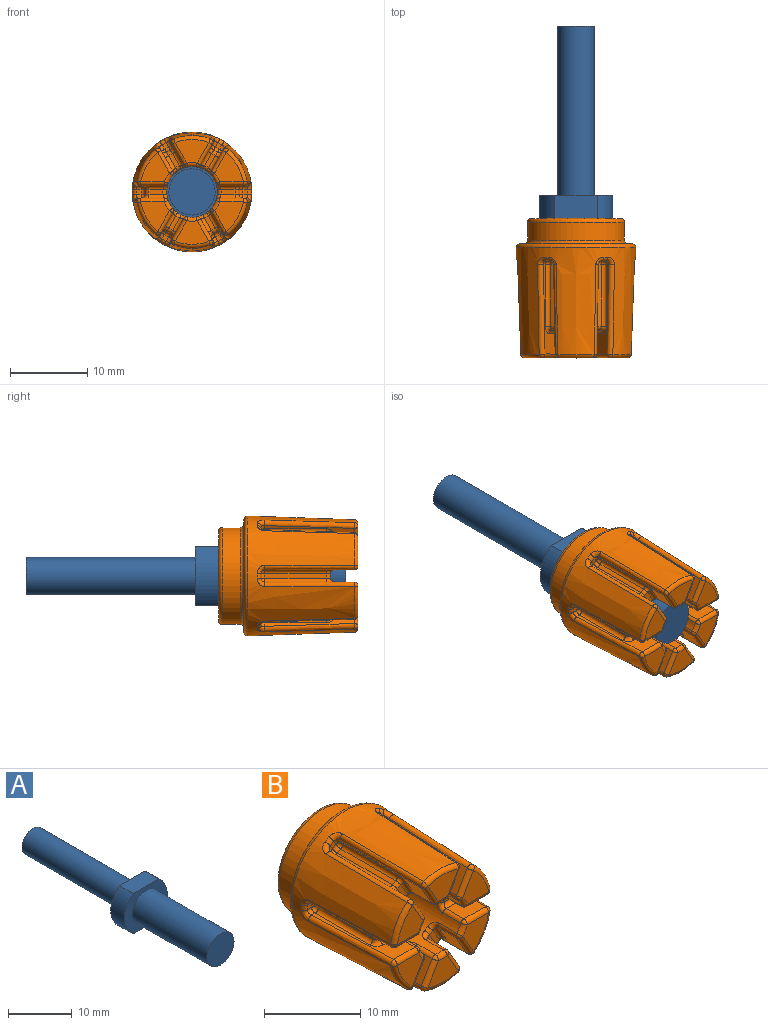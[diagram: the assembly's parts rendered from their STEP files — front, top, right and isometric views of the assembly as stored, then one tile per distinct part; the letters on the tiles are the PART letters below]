
ASSEMBLY  parts=2 mates=1
PART A: 10 faces, bbox 9.5x41.5x7.7 mm
  f0: plane 5.56x3mm, normal (0,0,-1), area 16.7mm2, adj f1,f2,f3,f4
  f1: cylinder r=4.75mm len=7.7mm, axis (0,1,0), area 26.9mm2, adj f0,f3,f4,f5
  f2: cylinder r=4.75mm len=7.7mm, axis (0,1,0), area 26.9mm2, adj f0,f3,f4,f5
  f3: plane 9.5x7.7mm, normal (0,-1,0), area 35.8mm2, adj f0,f1,f2,f5,f8
  f4: plane 9.5x7.7mm, normal (0,1,0), area 46mm2, adj f0,f1,f2,f5,f6
  f5: plane 5.56x3mm, normal (0,0,1), area 16.7mm2, adj f1,f2,f3,f4
  f6: cylinder r=2.4mm len=22mm, axis (0,-1,0), area 331.8mm2, adj f4,f7
  f7: plane 4.8x4.8mm, normal (0,1,0), area 18.1mm2, adj f6
  f8: cylinder r=3mm len=16.5mm, axis (0,1,0), area 311mm2, adj f3,f9
  f9: plane 6x6mm, normal (0,-1,0), area 28.3mm2, adj f8
PART B: 225 faces, bbox 16.8x20.8x16.8 mm
  f0: cone r=7.8mm half-angle=2deg, axis (0,1,0), area 445mm2, adj f49,f50,f53,f54,f58,f63,f69,f75
  f1: plane 11.6x3.05mm, normal (-0.87,0,0.5), area 11.4mm2, adj f194,f195,f207,f208,f213,f216,f217
  f2: plane 11.6x3.05mm, normal (0.87,0,-0.5), area 11.4mm2, adj f186,f187,f203,f204,f210,f214,f215
  f3: plane 1.86x1.42mm, normal (0,-1,0), area 1.1mm2, adj f209,f214,f217,f220
  f4: plane 1.81x0.6mm, normal (0,-1,0), area 1.1mm2, adj f158,f159,f174,f175
  f5: plane 1.86x1.42mm, normal (0,-1,0), area 1.1mm2, adj f98,f99,f114,f115
  f6: plane 1.86x1.42mm, normal (0,-1,0), area 1.1mm2, adj f46,f55,f56,f57
  f7: plane 1.81x0.6mm, normal (0,-1,0), area 1.1mm2, adj f102,f103,f116,f117
  f8: plane 11.6x3.05mm, normal (0.87,0,0.5), area 11.4mm2, adj f164,f165,f171,f177,f178,f191,f192
  f9: plane 11.6x3.05mm, normal (-0.87,0,-0.5), area 11.4mm2, adj f142,f143,f145,f146,f152,f161,f162
  f10: plane 11.6x3.52mm, normal (0,0,-1), area 11.4mm2, adj f82,f83,f85,f86,f92,f101,f102
  f11: plane 11.6x3.05mm, normal (-0.87,0,0.5), area 11.4mm2, adj f47,f48,f52,f57,f58,f66,f67
  f12: plane 11.6x3.05mm, normal (0.87,0,-0.5), area 11.4mm2, adj f44,f45,f51,f54,f55,f64,f65
  f13: plane 11.6x3.05mm, normal (-0.87,0,-0.5), area 11.4mm2, adj f75,f76,f78,f79,f89,f99,f100
  f14: plane 11.6x3.05mm, normal (0.87,0,0.5), area 11.4mm2, adj f96,f97,f108,f113,f114,f124,f125
  f15: plane 4.42x3.06mm, normal (0,-1,0), area 8.8mm2, adj f192,f193,f206,f207
  f16: plane 11.6x3.52mm, normal (0,0,1), area 11.4mm2, adj f104,f105,f111,f117,f118,f126,f127
  f17: plane 3.83x3.76mm, normal (0,-1,0), area 8.8mm2, adj f127,f129,f141,f142
  f18: plane 3.83x3.76mm, normal (0,-1,0), area 8.8mm2, adj f67,f69,f81,f82
  f19: plane 4.42x3.06mm, normal (0,-1,0), area 8.8mm2, adj f63,f64,f79,f80
  f20: plane 11.6x3.52mm, normal (0,0,-1), area 11.4mm2, adj f135,f136,f138,f139,f149,f159,f160
  f21: plane 3.83x3.76mm, normal (0,-1,0), area 8.8mm2, adj f123,f124,f139,f140
  f22: plane 11.6x3.52mm, normal (0,0,1), area 11.4mm2, adj f156,f157,f168,f173,f174,f189,f190
  f23: plane 3.83x3.76mm, normal (0,-1,0), area 8.8mm2, adj f188,f189,f204,f205
  f24: plane 0.86x0.84mm, normal (0,-1,0), area 0.4mm2, adj f179,f186,f195,f196
  f25: plane 1.86x1.42mm, normal (0,-1,0), area 1.1mm2, adj f162,f163,f176,f177
  f26: plane 0.86x0.84mm, normal (0,-1,0), area 0.4mm2, adj f144,f145,f165,f166
  f27: plane 0.65x0.6mm, normal (0,-1,0), area 0.4mm2, adj f84,f85,f105,f106
  f28: plane 0.86x0.84mm, normal (0,-1,0), area 0.4mm2, adj f41,f44,f48,f49
  f29: plane 0.86x0.84mm, normal (0,-1,0), area 0.4mm2, adj f76,f77,f95,f96
  f30: plane 0.65x0.6mm, normal (0,-1,0), area 0.4mm2, adj f136,f137,f155,f156
  f31: cylinder r=6.3mm len=12.6mm, axis (0,1,0), area 91mm2, adj f223,f224
  f32: plane 11.6x11.6mm, normal (0,1,0), area 60.3mm2, adj f221,f223
  f33: plane 14.56x14.56mm, normal (0,1,0), area 21.3mm2, adj f222,f224
  f34: cylinder r=6.1mm len=8mm, axis (0,1,0), area 4.4mm2, adj f137,f138,f157,f158
  f35: cylinder r=6.1mm len=8mm, axis (0,1,0), area 4.4mm2, adj f77,f78,f97,f98
  f36: cylinder r=6.1mm len=8mm, axis (0,1,0), area 4.4mm2, adj f41,f45,f46,f47
  f37: cylinder r=6.1mm len=8mm, axis (0,1,0), area 4.4mm2, adj f83,f84,f103,f104
  f38: cylinder r=6.1mm len=8mm, axis (0,1,0), area 4.4mm2, adj f143,f144,f163,f164
  f39: cylinder r=6.1mm len=8mm, axis (0,1,0), area 4.4mm2, adj f196,f203,f208,f209
  f40: cylinder r=3.3mm len=17.1mm, axis (0,1,0), area 307.1mm2, adj f56,f60,f61,f65,f66,f80,f81,f100
  f41: torus R=6.6mm, axis (0,-1,0), area 0.4mm2, adj f28,f36,f42,f43
  f42: sphere r=0.5mm, area 0.4mm2, adj f41,f44,f45
  f43: sphere r=0.5mm, area 0.4mm2, adj f41,f47,f48
  f44: cylinder r=0.5mm len=0.81mm, axis (-0.5,0,-0.87), area 0.4mm2, adj f12,f28,f42,f50
  f45: cylinder r=0.5mm len=8mm, axis (0,1,0), area 6.5mm2, adj f12,f36,f42,f51
  f46: torus R=5.6mm, axis (0,-1,0), area 0.5mm2, adj f6,f36,f51,f52
  f47: cylinder r=0.5mm len=8mm, axis (0,1,0), area 6.5mm2, adj f11,f36,f43,f52
  f48: cylinder r=0.5mm len=0.81mm, axis (0.5,0,0.87), area 0.4mm2, adj f11,f28,f43,f53
  f49: torus R=7.24mm, axis (0,-1,0), area 0.5mm2, adj f0,f28,f50,f53
  f50: bspline ~1.22x1.16mm, area 0.9mm2, adj f0,f44,f49,f54
  f51: bspline ~1.21x1.17mm, area 0.9mm2, adj f12,f45,f46,f55
  f52: bspline ~1.22x1.02mm, area 0.9mm2, adj f11,f46,f47,f57
  f53: bspline ~1.21x1.17mm, area 0.9mm2, adj f0,f48,f49,f58
  f54: bspline ~18.06x1.28mm, area 10.2mm2, adj f0,f12,f50,f59
  f55: cylinder r=0.5mm len=2mm, axis (-0.5,0,-0.87), area 1.5mm2, adj f6,f12,f51,f60
  f56: torus R=3.8mm, axis (0,-1,0), area 0.4mm2, adj f6,f40,f60,f61
  f57: cylinder r=0.5mm len=2mm, axis (0.5,0,0.87), area 1.5mm2, adj f6,f11,f52,f61
  f58: bspline ~18.06x1.08mm, area 10.2mm2, adj f0,f11,f53,f62
  f59: sphere r=0.5mm, area 0.4mm2, adj f54,f63,f64
  f60: bspline ~1.17x1.16mm, area 0.7mm2, adj f40,f55,f56,f65
  f61: bspline ~1.21x1.05mm, area 0.7mm2, adj f40,f56,f57,f66
  f62: sphere r=0.5mm, area 0.4mm2, adj f58,f67,f69
  f63: torus R=6.8mm, axis (0,-1,0), area 3.6mm2, adj f0,f19,f59,f70
  f64: cylinder r=0.5mm len=2.94mm, axis (0.5,0,0.87), area 2.4mm2, adj f12,f19,f59,f71
  f65: cylinder r=0.5mm len=2.6mm, axis (0,1,0), area 1.6mm2, adj f12,f40,f60,f71
  f66: cylinder r=0.5mm len=2.6mm, axis (0,1,0), area 1.6mm2, adj f11,f40,f61,f73
  f67: cylinder r=0.5mm len=2.94mm, axis (-0.5,0,-0.87), area 2.4mm2, adj f11,f18,f62,f73
  f68: sphere r=0.5mm, area 0.4mm2, adj f76,f77,f78
  f69: torus R=6.8mm, axis (0,-1,0), area 3.6mm2, adj f0,f18,f62,f74
  f70: sphere r=0.5mm, area 0.4mm2, adj f63,f75,f79
  f71: sphere r=0.5mm, area 0.3mm2, adj f64,f65,f80
  f72: sphere r=0.5mm, area 0.4mm2, adj f83,f84,f85
  f73: sphere r=0.5mm, area 0.3mm2, adj f66,f67,f81
  f74: sphere r=0.5mm, area 0.4mm2, adj f69,f82,f86
  f75: bspline ~18.06x1.28mm, area 10.2mm2, adj f0,f13,f70,f87
  f76: cylinder r=0.5mm len=0.81mm, axis (-0.5,0,0.87), area 0.4mm2, adj f13,f29,f68,f87
  f77: torus R=6.6mm, axis (0,-1,0), area 0.4mm2, adj f29,f35,f68,f88
  f78: cylinder r=0.5mm len=8mm, axis (0,1,0), area 6.5mm2, adj f13,f35,f68,f89
  f79: cylinder r=0.5mm len=2.94mm, axis (0.5,0,-0.87), area 2.4mm2, adj f13,f19,f70,f90
  f80: torus R=3.8mm, axis (0,-1,0), area 1mm2, adj f19,f40,f71,f90
  f81: torus R=3.8mm, axis (0,-1,0), area 1mm2, adj f18,f40,f73,f91
  f82: cylinder r=0.5mm len=3.1mm, axis (1,0,0), area 2.4mm2, adj f10,f18,f74,f91
  f83: cylinder r=0.5mm len=8mm, axis (0,1,0), area 6.5mm2, adj f10,f37,f72,f92
  f84: torus R=6.6mm, axis (0,-1,0), area 0.4mm2, adj f27,f37,f72,f93
  f85: cylinder r=0.5mm len=0.64mm, axis (-1,0,0), area 0.4mm2, adj f10,f27,f72,f94
  f86: bspline ~18.06x1.24mm, area 10.2mm2, adj f0,f10,f74,f94
  f87: bspline ~1.21x1.17mm, area 0.9mm2, adj f0,f75,f76,f95
  f88: sphere r=0.5mm, area 0.4mm2, adj f77,f96,f97
  f89: bspline ~1.22x1.19mm, area 0.9mm2, adj f13,f78,f98,f99
  f90: sphere r=0.5mm, area 0.3mm2, adj f79,f80,f100
  f91: sphere r=0.5mm, area 0.3mm2, adj f81,f82,f101
  f92: bspline ~1.23x1.17mm, area 0.9mm2, adj f10,f83,f102,f103
  f93: sphere r=0.5mm, area 0.4mm2, adj f84,f104,f105
  f94: bspline ~1.25x1.22mm, area 0.9mm2, adj f0,f85,f86,f106
  f95: torus R=7.24mm, axis (0,-1,0), area 0.5mm2, adj f0,f29,f87,f107
  f96: cylinder r=0.5mm len=0.81mm, axis (0.5,0,-0.87), area 0.4mm2, adj f14,f29,f88,f107
  f97: cylinder r=0.5mm len=8mm, axis (0,1,0), area 6.5mm2, adj f14,f35,f88,f108
  f98: torus R=5.6mm, axis (0,-1,0), area 0.5mm2, adj f5,f35,f89,f108
  f99: cylinder r=0.5mm len=2mm, axis (-0.5,0,0.87), area 1.5mm2, adj f5,f13,f89,f109
  f100: cylinder r=0.5mm len=2.6mm, axis (0,1,0), area 1.6mm2, adj f13,f40,f90,f109
  f101: cylinder r=0.5mm len=2.6mm, axis (0,1,0), area 1.6mm2, adj f10,f40,f91,f110
  f102: cylinder r=0.5mm len=2.02mm, axis (-1,0,0), area 1.5mm2, adj f7,f10,f92,f110
  f103: torus R=5.6mm, axis (0,-1,0), area 0.5mm2, adj f7,f37,f92,f111
  f104: cylinder r=0.5mm len=8mm, axis (0,1,0), area 6.5mm2, adj f16,f37,f93,f111
  f105: cylinder r=0.5mm len=0.64mm, axis (-1,0,0), area 0.4mm2, adj f16,f27,f93,f112
  f106: torus R=7.24mm, axis (0,-1,0), area 0.5mm2, adj f0,f27,f94,f112
  f107: bspline ~1.22x1.19mm, area 0.9mm2, adj f0,f95,f96,f113
  f108: bspline ~1.17x1.06mm, area 0.9mm2, adj f14,f97,f98,f114
  f109: bspline ~1.21x1.13mm, area 0.7mm2, adj f40,f99,f100,f115
  f110: bspline ~1.17x1.06mm, area 0.7mm2, adj f40,f101,f102,f116
  f111: bspline ~1.22x1.17mm, area 0.9mm2, adj f16,f103,f104,f117
  f112: bspline ~1.31x1.17mm, area 0.9mm2, adj f0,f105,f106,f118
  f113: bspline ~18.06x1.08mm, area 10.2mm2, adj f0,f14,f107,f119
  f114: cylinder r=0.5mm len=2mm, axis (0.5,0,-0.87), area 1.5mm2, adj f5,f14,f108,f120
  f115: torus R=3.8mm, axis (0,-1,0), area 0.4mm2, adj f5,f40,f109,f120
  f116: torus R=3.8mm, axis (0,-1,0), area 0.4mm2, adj f7,f40,f110,f121
  f117: cylinder r=0.5mm len=2.02mm, axis (-1,0,0), area 1.5mm2, adj f7,f16,f111,f121
  f118: bspline ~18.06x1.24mm, area 10.2mm2, adj f0,f16,f112,f122
  f119: sphere r=0.5mm, area 0.4mm2, adj f113,f123,f124
  f120: bspline ~1.17x1.07mm, area 0.7mm2, adj f40,f114,f115,f125
  f121: bspline ~1.21x1mm, area 0.7mm2, adj f40,f116,f117,f126
  f122: sphere r=0.5mm, area 0.4mm2, adj f118,f127,f129
  f123: torus R=6.8mm, axis (0,-1,0), area 3.6mm2, adj f0,f21,f119,f130
  f124: cylinder r=0.5mm len=2.94mm, axis (-0.5,0,0.87), area 2.4mm2, adj f14,f21,f119,f131
  f125: cylinder r=0.5mm len=2.6mm, axis (0,1,0), area 1.6mm2, adj f14,f40,f120,f131
  f126: cylinder r=0.5mm len=2.6mm, axis (0,1,0), area 1.6mm2, adj f16,f40,f121,f133
  f127: cylinder r=0.5mm len=3.1mm, axis (-1,0,0), area 2.4mm2, adj f16,f17,f122,f133
  f128: sphere r=0.5mm, area 0.4mm2, adj f136,f137,f138
  f129: torus R=6.8mm, axis (0,-1,0), area 3.6mm2, adj f0,f17,f122,f134
  f130: sphere r=0.5mm, area 0.4mm2, adj f123,f135,f139
  f131: sphere r=0.5mm, area 0.3mm2, adj f124,f125,f140
  f132: sphere r=0.5mm, area 0.4mm2, adj f143,f144,f145
  f133: sphere r=0.5mm, area 0.3mm2, adj f126,f127,f141
  f134: sphere r=0.5mm, area 0.4mm2, adj f129,f142,f146
  f135: bspline ~18.06x1.24mm, area 10.2mm2, adj f0,f20,f130,f147
  f136: cylinder r=0.5mm len=0.64mm, axis (-1,0,0), area 0.4mm2, adj f20,f30,f128,f147
  f137: torus R=6.6mm, axis (0,-1,0), area 0.4mm2, adj f30,f34,f128,f148
  f138: cylinder r=0.5mm len=8mm, axis (0,1,0), area 6.5mm2, adj f20,f34,f128,f149
  f139: cylinder r=0.5mm len=3.1mm, axis (1,0,0), area 2.4mm2, adj f20,f21,f130,f150
  f140: torus R=3.8mm, axis (0,-1,0), area 1mm2, adj f21,f40,f131,f150
  f141: torus R=3.8mm, axis (0,-1,0), area 1mm2, adj f17,f40,f133,f151
  f142: cylinder r=0.5mm len=2.94mm, axis (0.5,0,-0.87), area 2.4mm2, adj f9,f17,f134,f151
  f143: cylinder r=0.5mm len=8mm, axis (0,1,0), area 6.5mm2, adj f9,f38,f132,f152
  f144: torus R=6.6mm, axis (0,-1,0), area 0.4mm2, adj f26,f38,f132,f153
  f145: cylinder r=0.5mm len=0.81mm, axis (-0.5,0,0.87), area 0.4mm2, adj f9,f26,f132,f154
  f146: bspline ~18.06x1.08mm, area 10.2mm2, adj f0,f9,f134,f154
  f147: bspline ~1.31x1.17mm, area 0.9mm2, adj f0,f135,f136,f155
  f148: sphere r=0.5mm, area 0.4mm2, adj f137,f156,f157
  f149: bspline ~1.22x1.17mm, area 0.9mm2, adj f20,f138,f158,f159
  f150: sphere r=0.5mm, area 0.3mm2, adj f139,f140,f160
  f151: sphere r=0.5mm, area 0.3mm2, adj f141,f142,f161
  f152: bspline ~1.17x1.06mm, area 0.9mm2, adj f9,f143,f162,f163
  f153: sphere r=0.5mm, area 0.4mm2, adj f144,f164,f165
  f154: bspline ~1.22x1.19mm, area 0.9mm2, adj f0,f145,f146,f166
  f155: torus R=7.24mm, axis (0,-1,0), area 0.5mm2, adj f0,f30,f147,f167
  f156: cylinder r=0.5mm len=0.64mm, axis (1,0,0), area 0.4mm2, adj f22,f30,f148,f167
  f157: cylinder r=0.5mm len=8mm, axis (0,1,0), area 6.5mm2, adj f22,f34,f148,f168
  f158: torus R=5.6mm, axis (0,-1,0), area 0.5mm2, adj f4,f34,f149,f168
  f159: cylinder r=0.5mm len=2.02mm, axis (-1,0,0), area 1.5mm2, adj f4,f20,f149,f169
  f160: cylinder r=0.5mm len=2.6mm, axis (0,1,0), area 1.6mm2, adj f20,f40,f150,f169
  f161: cylinder r=0.5mm len=2.6mm, axis (0,1,0), area 1.6mm2, adj f9,f40,f151,f170
  f162: cylinder r=0.5mm len=2mm, axis (-0.5,0,0.87), area 1.5mm2, adj f9,f25,f152,f170
  f163: torus R=5.6mm, axis (0,-1,0), area 0.5mm2, adj f25,f38,f152,f171
  f164: cylinder r=0.5mm len=8mm, axis (0,1,0), area 6.5mm2, adj f8,f38,f153,f171
  f165: cylinder r=0.5mm len=0.81mm, axis (0.5,0,-0.87), area 0.4mm2, adj f8,f26,f153,f172
  f166: torus R=7.24mm, axis (0,-1,0), area 0.5mm2, adj f0,f26,f154,f172
  f167: bspline ~1.25x1.22mm, area 0.9mm2, adj f0,f155,f156,f173
  f168: bspline ~1.23x1.17mm, area 0.9mm2, adj f22,f157,f158,f174
  f169: bspline ~1.21x1mm, area 0.7mm2, adj f40,f159,f160,f175
  f170: bspline ~1.17x1.07mm, area 0.7mm2, adj f40,f161,f162,f176
  f171: bspline ~1.22x1.19mm, area 0.9mm2, adj f8,f163,f164,f177
  f172: bspline ~1.21x1.17mm, area 0.9mm2, adj f0,f165,f166,f178
  f173: bspline ~18.06x1.24mm, area 10.2mm2, adj f0,f22,f167,f181
  f174: cylinder r=0.5mm len=2.02mm, axis (1,0,0), area 1.5mm2, adj f4,f22,f168,f182
  f175: torus R=3.8mm, axis (0,-1,0), area 0.4mm2, adj f4,f40,f169,f182
  f176: torus R=3.8mm, axis (0,-1,0), area 0.4mm2, adj f25,f40,f170,f183
  f177: cylinder r=0.5mm len=2mm, axis (0.5,0,-0.87), area 1.5mm2, adj f8,f25,f171,f183
  f178: bspline ~18.06x1.28mm, area 10.2mm2, adj f0,f8,f172,f184
  f179: torus R=7.24mm, axis (0,-1,0), area 0.5mm2, adj f0,f24,f180,f185
  f180: bspline ~1.21x1.17mm, area 0.9mm2, adj f0,f179,f186,f187
  f181: sphere r=0.5mm, area 0.4mm2, adj f173,f188,f189
  f182: bspline ~1.17x1.06mm, area 0.7mm2, adj f40,f174,f175,f190
  f183: bspline ~1.21x1.13mm, area 0.7mm2, adj f40,f176,f177,f191
  f184: sphere r=0.5mm, area 0.4mm2, adj f178,f192,f193
  f185: bspline ~1.16x1.06mm, area 0.9mm2, adj f0,f179,f194,f195
  f186: cylinder r=0.5mm len=0.81mm, axis (-0.5,0,-0.87), area 0.4mm2, adj f2,f24,f180,f197
  f187: bspline ~18.06x1.08mm, area 10.2mm2, adj f0,f2,f180,f198
  f188: torus R=6.8mm, axis (0,-1,0), area 3.6mm2, adj f0,f23,f181,f198
  f189: cylinder r=0.5mm len=3.1mm, axis (-1,0,0), area 2.4mm2, adj f22,f23,f181,f199
  f190: cylinder r=0.5mm len=2.6mm, axis (0,1,0), area 1.6mm2, adj f22,f40,f182,f199
  f191: cylinder r=0.5mm len=2.6mm, axis (0,1,0), area 1.6mm2, adj f8,f40,f183,f200
  f192: cylinder r=0.5mm len=2.94mm, axis (-0.5,0,0.87), area 2.4mm2, adj f8,f15,f184,f200
  f193: torus R=6.8mm, axis (0,-1,0), area 3.6mm2, adj f0,f15,f184,f201
  f194: bspline ~18.06x1.28mm, area 10.2mm2, adj f0,f1,f185,f201
  f195: cylinder r=0.5mm len=0.81mm, axis (0.5,0,0.87), area 0.4mm2, adj f1,f24,f185,f202
  f196: torus R=6.6mm, axis (0,-1,0), area 0.4mm2, adj f24,f39,f197,f202
  f197: sphere r=0.5mm, area 0.4mm2, adj f186,f196,f203
  f198: sphere r=0.5mm, area 0.4mm2, adj f187,f188,f204
  f199: sphere r=0.5mm, area 0.3mm2, adj f189,f190,f205
  f200: sphere r=0.5mm, area 0.3mm2, adj f191,f192,f206
  f201: sphere r=0.5mm, area 0.4mm2, adj f193,f194,f207
  f202: sphere r=0.5mm, area 0.4mm2, adj f195,f196,f208
  f203: cylinder r=0.5mm len=8mm, axis (0,1,0), area 6.5mm2, adj f2,f39,f197,f210
  f204: cylinder r=0.5mm len=2.94mm, axis (0.5,0,0.87), area 2.4mm2, adj f2,f23,f198,f211
  f205: torus R=3.8mm, axis (0,-1,0), area 1mm2, adj f23,f40,f199,f211
  f206: torus R=3.8mm, axis (0,-1,0), area 1mm2, adj f15,f40,f200,f212
  f207: cylinder r=0.5mm len=2.94mm, axis (-0.5,0,-0.87), area 2.4mm2, adj f1,f15,f201,f212
  f208: cylinder r=0.5mm len=8mm, axis (0,1,0), area 6.5mm2, adj f1,f39,f202,f213
  f209: torus R=5.6mm, axis (0,-1,0), area 0.5mm2, adj f3,f39,f210,f213
  f210: bspline ~1.22x1.02mm, area 0.9mm2, adj f2,f203,f209,f214
  f211: sphere r=0.5mm, area 0.3mm2, adj f204,f205,f215
  f212: sphere r=0.5mm, area 0.3mm2, adj f206,f207,f216
  f213: bspline ~1.21x1.17mm, area 0.9mm2, adj f1,f208,f209,f217
  f214: cylinder r=0.5mm len=2mm, axis (-0.5,0,-0.87), area 1.5mm2, adj f2,f3,f210,f218
  f215: cylinder r=0.5mm len=2.6mm, axis (0,1,0), area 1.6mm2, adj f2,f40,f211,f218
  f216: cylinder r=0.5mm len=2.6mm, axis (0,1,0), area 1.6mm2, adj f1,f40,f212,f219
  f217: cylinder r=0.5mm len=2mm, axis (0.5,0,0.87), area 1.5mm2, adj f1,f3,f213,f219
  f218: bspline ~1.21x1.05mm, area 0.7mm2, adj f40,f214,f215,f220
  f219: bspline ~1.17x1.16mm, area 0.7mm2, adj f40,f216,f217,f220
  f220: torus R=3.8mm, axis (0,-1,0), area 0.4mm2, adj f3,f40,f218,f219
  f221: torus R=3.8mm, axis (0,-1,0), area 17.2mm2, adj f32,f40
  f222: torus R=7.28mm, axis (0,-1,0), area 38.4mm2, adj f0,f33
  f223: torus R=5.8mm, axis (0,-1,0), area 30.2mm2, adj f31,f32
  f224: torus R=6.8mm, axis (0,-1,0), area 32mm2, adj f31,f33
PLACE A t=(0,3,0)mm
PLACE B at identity
MATE fastened B.f40 <-> A.f8  axis (0,1,0) through (0,0,0)mm
